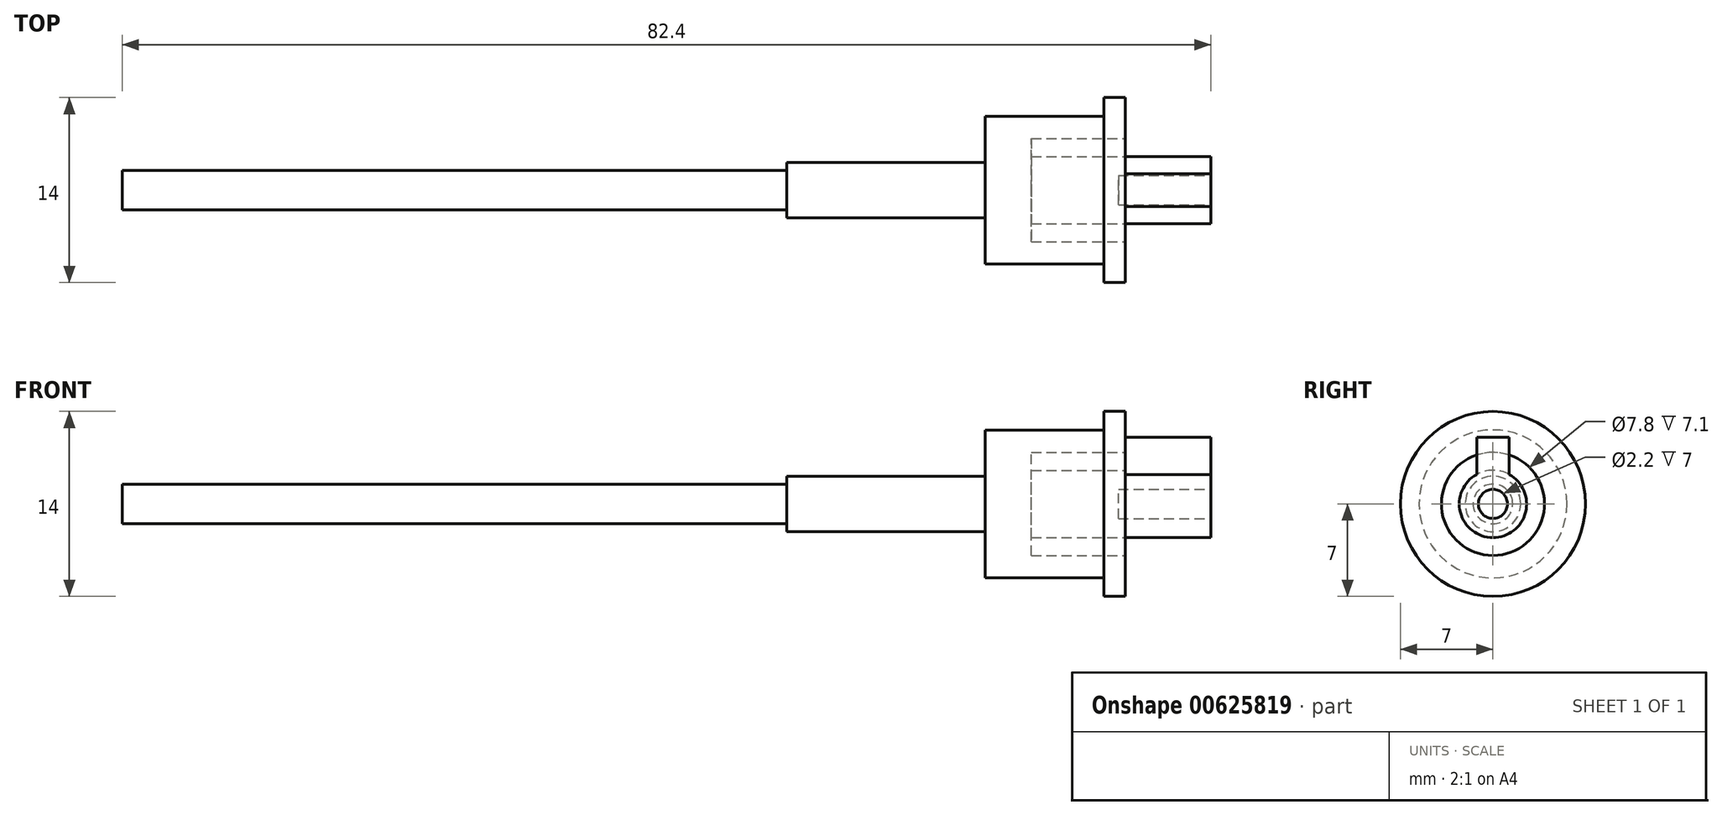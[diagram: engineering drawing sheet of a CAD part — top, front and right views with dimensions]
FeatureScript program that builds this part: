
annotation { "Feature Type Name" : "Feature", "Feature Type Description" : "" }
export const myFeature = defineFeature(function(context is Context, id is Id, definition is map)
    precondition{}
    {
        {
            var Q0;
            Q0=qCreatedBy(makeId("Front.planeOp"),FACE);
            var sketch = newSketch(context, id + "F0", { "sketchPlane" : qUnion([Q0])});
            skLineSegment(sketch, "E0", {"start": v(-32.16, 28.06) * mm, "end": v(18.14, 28.06) * mm});
            skLineSegment(sketch, "E1", {"start": v(18.14, 28.06) * mm, "end": v(18.14, 28.66) * mm});
            skLineSegment(sketch, "E2", {"start": v(18.14, 28.66) * mm, "end": v(33.14, 28.66) * mm});
            skLineSegment(sketch, "E3", {"start": v(33.14, 28.66) * mm, "end": v(33.14, 32.16) * mm});
            skLineSegment(sketch, "E4", {"start": v(33.14, 32.16) * mm, "end": v(42.14, 32.16) * mm});
            skLineSegment(sketch, "E5", {"start": v(42.14, 32.16) * mm, "end": v(42.14, 33.56) * mm});
            skLineSegment(sketch, "E6", {"start": v(42.14, 33.56) * mm, "end": v(43.74, 33.56) * mm});
            skLineSegment(sketch, "E7", {"start": v(43.74, 33.56) * mm, "end": v(43.74, 30.46) * mm});
            skLineSegment(sketch, "E8", {"start": v(43.74, 30.46) * mm, "end": v(36.64, 30.46) * mm});
            skLineSegment(sketch, "E9", {"start": v(36.64, 30.46) * mm, "end": v(36.64, 29.11) * mm});
            skLineSegment(sketch, "E10", {"start": v(36.64, 29.11) * mm, "end": v(50.24, 29.11) * mm});
            skLineSegment(sketch, "E11", {"start": v(50.24, 29.11) * mm, "end": v(50.24, 26.56) * mm});
            skLineSegment(sketch, "E12", {"start": v(50.24, 26.56) * mm, "end": v(-32.16, 26.56) * mm});
            skLineSegment(sketch, "E13", {"start": v(-32.16, 26.56) * mm, "end": v(-32.16, 28.06) * mm});
            skSolve(sketch);
        }
        {
            var Q0;
            Q0=makeQuery(id+"F0.imprint","IMPRINT",FACE,{"disambiguationData":[TD([[makeQuery(id+"F0.imprint","IMPRINT",EDGE,{"derivedFrom":sQuery(id+"F0.wireOp",EDGE,"E0")}),-1.0]])]});
            var Q1;
            Q1=sQuery(id+"F0.wireOp",EDGE,"E12");
            revolve(context, id + "F1", {"entities" : qUnion([Q0]), "axis" : qUnion([Q1]), "revolveType" : RevolveType.FULL});
        }
        {
            var Q0;
            Q0=makeQuery(id+"F1.opRevolve","SWEPT_FACE",FACE,{"disambiguationData":[OSD([sQuery(id+"F0.wireOp",EDGE,"E11")])]});
            var sketch = newSketch(context, id + "F2", { "sketchPlane" : qUnion([Q0])});
            skCircle(sketch, "E14", {"center": v(0, 26.56) * mm, "radius": 1.1 * mm});
            skSolve(sketch);
        }
        {
            var Q0;
            Q0 = qSketchRegion(id + "F2", true);
            extrude(context, id + "F3", {"entities" : qUnion([Q0]), "operationType" : NewBodyOperationType.REMOVE, "oppositeDirection" : true, "depth" : 7 * mm, "offsetDistance" : 25 * mm});
        }
        {
            var Q0;
            Q0=makeQuery(id+"F1.opRevolve","SWEPT_FACE",FACE,{"disambiguationData":[OSD([sQuery(id+"F0.wireOp",EDGE,"E11")])]});
            var sketch = newSketch(context, id + "F4", { "sketchPlane" : qUnion([Q0])});
            skLineSegment(sketch, "E15", {"start": v(-1.23, 28.8) * mm, "end": v(-1.23, 31.6) * mm});
            skLineSegment(sketch, "E16", {"start": v(-1.23, 31.6) * mm, "end": v(1.23, 31.6) * mm});
            skLineSegment(sketch, "E17", {"start": v(1.23, 31.6) * mm, "end": v(1.23, 28.8) * mm});
            skSolve(sketch);
        }
        {
            var Q0;
            {var subQ0=sQuery(id+"F4.wireOp",EDGE,"E15");Q0=makeQuery(id+"F4.imprint","IMPRINT",FACE,{"disambiguationData":[TD([[makeQuery(id+"F4.imprint","IMPRINT",EDGE,{"derivedFrom":subQ0}),-1.0]])]});}
            var Q1;
            Q1=makeQuery(id+"F1.opRevolve","SWEPT_FACE",FACE,{"disambiguationData":[OSD([sQuery(id+"F0.wireOp",EDGE,"E7")])]});
            extrude(context, id + "F5", {"entities" : qUnion([Q0]), "operationType" : NewBodyOperationType.ADD, "endBound" : BoundingType.UP_TO_SURFACE, "oppositeDirection" : true, "depth" : 25 * mm, "endBoundEntityFace" : qUnion([Q1]), "offsetDistance" : 25 * mm});
        }
    });
